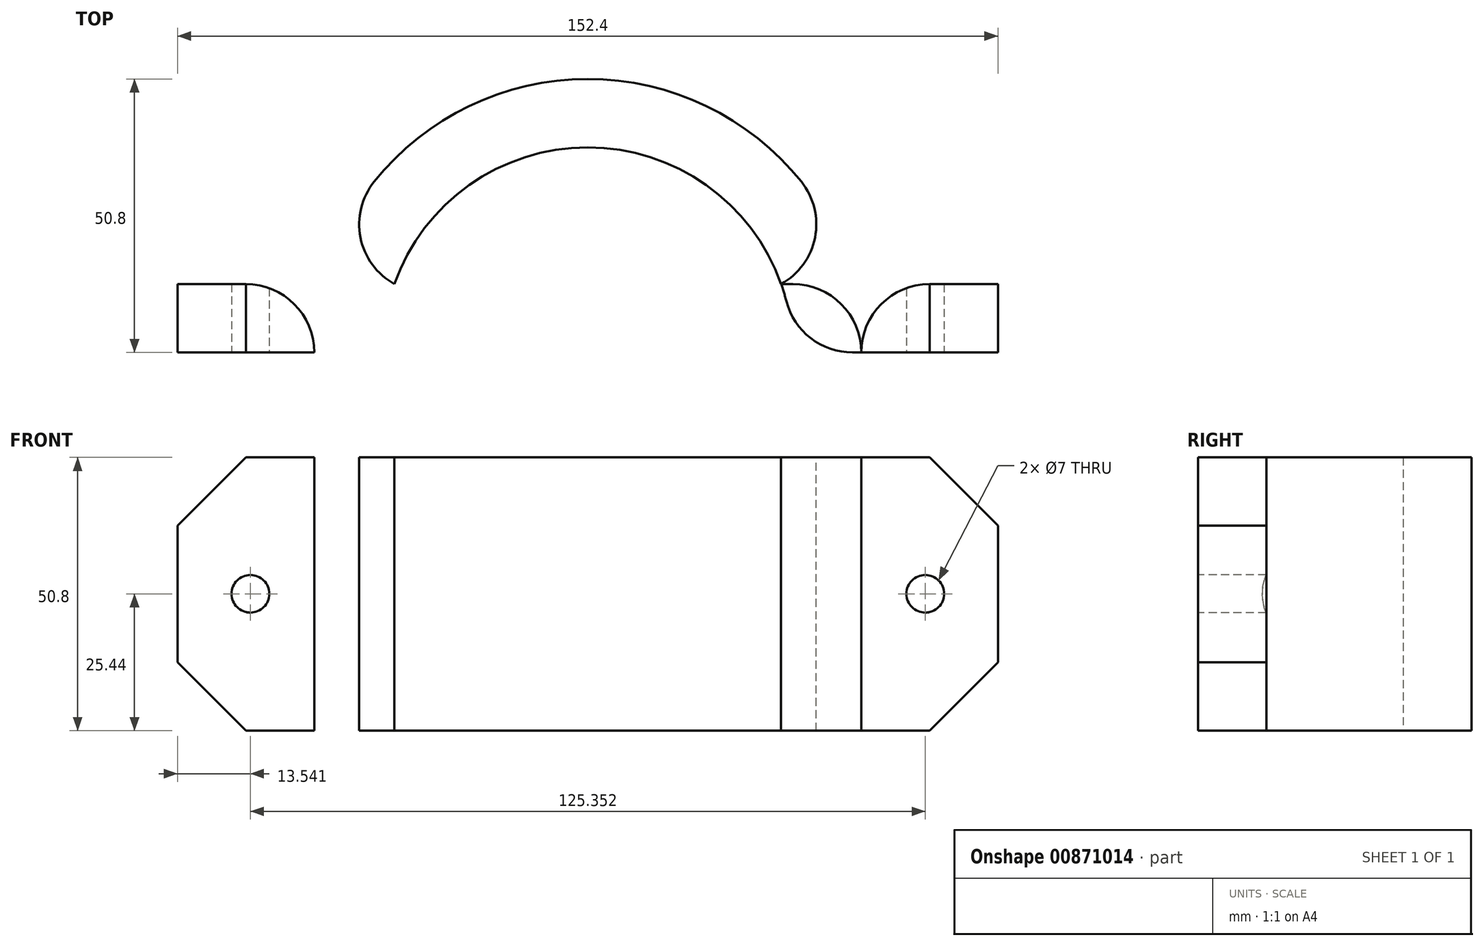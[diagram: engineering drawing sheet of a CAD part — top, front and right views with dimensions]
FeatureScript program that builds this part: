
annotation { "Feature Type Name" : "Feature", "Feature Type Description" : "" }
export const myFeature = defineFeature(function(context is Context, id is Id, definition is map)
    precondition{}
    {
        {
            var Q0;
            Q0=qCreatedBy(makeId("Top.planeOp"),FACE);
            var sketch = newSketch(context, id + "F0", { "sketchPlane" : qUnion([Q0])});
            skCircle(sketch, "E0", {"center": v(0, 0) * mm, "radius": 38.1 * mm});
            skCircle(sketch, "E1", {"center": v(0, 0) * mm, "radius": 50.8 * mm});
            skLineSegment(sketch, "E2.bottom", {"start": v(76.2, -12.7) * mm, "end": v(-76.2, -12.7) * mm});
            skLineSegment(sketch, "E2.top", {"start": v(76.2, 12.7) * mm, "end": v(-76.2, 12.7) * mm});
            skLineSegment(sketch, "E2.left", {"start": v(76.2, -12.7) * mm, "end": v(76.2, 12.7) * mm});
            skLineSegment(sketch, "E2.right", {"start": v(-76.2, -12.7) * mm, "end": v(-76.2, 12.7) * mm});
            skPoint(sketch, "E3", {"position": v(0, -50.8) * mm});
            skLineSegment(sketch, "E4.bottom", {"start": v(19.05, -12.7) * mm, "end": v(-19.05, -12.7) * mm});
            skLineSegment(sketch, "E4.top", {"start": v(19.05, -88.9) * mm, "end": v(-19.05, -88.9) * mm});
            skLineSegment(sketch, "E4.left", {"start": v(19.05, -12.7) * mm, "end": v(19.05, -88.9) * mm});
            skLineSegment(sketch, "E4.right", {"start": v(-19.05, -12.7) * mm, "end": v(-19.05, -88.9) * mm});
            skSolve(sketch);
        }
        {
            var Q0;
            {var subQ0=sQuery(id+"F0.wireOp",EDGE,"E2.top");var subQ1=sQuery(id+"F0.wireOp",EDGE,"E0");var subQ2=makeQuery(id+"F0.imprint","INTERSECT",VERTEX,{"disambiguationData":[OD(0.0)],"derivedFrom":[subQ1,subQ0]});Q0=makeQuery(id+"F0.imprint","IMPRINT",FACE,{"disambiguationData":[TD([[makeQuery(id+"F0.imprint","IMPRINT",EDGE,{"disambiguationData":[TD([[subQ2,1.0]])],"derivedFrom":subQ1}),-1.0]])]});}
            var Q1;
            {var subQ5=sQuery(id+"F0.wireOp",EDGE,"E2.right");Q1=makeQuery(id+"F0.imprint","IMPRINT",FACE,{"disambiguationData":[TD([[makeQuery(id+"F0.imprint","IMPRINT",EDGE,{"derivedFrom":subQ5}),-1.0]])]});}
            var Q2;
            {var subQ0=sQuery(id+"F0.wireOp",EDGE,"E2.top");var subQ1=sQuery(id+"F0.wireOp",EDGE,"E0");var subQ2=makeQuery(id+"F0.imprint","INTERSECT",VERTEX,{"disambiguationData":[OD(0.0)],"derivedFrom":[subQ1,subQ0]});Q2=makeQuery(id+"F0.imprint","IMPRINT",FACE,{"disambiguationData":[TD([[makeQuery(id+"F0.imprint","IMPRINT",EDGE,{"disambiguationData":[TD([[subQ2,-1.0]])],"derivedFrom":subQ1}),-1.0]])]});}
            var Q3;
            {var subQ0=sQuery(id+"F0.wireOp",EDGE,"E2.top");var subQ1=sQuery(id+"F0.wireOp",EDGE,"E0");var subQ2=makeQuery(id+"F0.imprint","INTERSECT",VERTEX,{"disambiguationData":[OD(1.0)],"derivedFrom":[subQ1,subQ0]});Q3=makeQuery(id+"F0.imprint","IMPRINT",FACE,{"disambiguationData":[TD([[makeQuery(id+"F0.imprint","IMPRINT",EDGE,{"disambiguationData":[TD([[subQ2,1.0]])],"derivedFrom":subQ1}),-1.0]])]});}
            var Q4;
            {var subQ5=sQuery(id+"F0.wireOp",EDGE,"E2.left");Q4=makeQuery(id+"F0.imprint","IMPRINT",FACE,{"disambiguationData":[TD([[makeQuery(id+"F0.imprint","IMPRINT",EDGE,{"derivedFrom":subQ5}),1.0]])]});}
            var Q5;
            {var subQ0=sQuery(id+"F0.wireOp",EDGE,"E2.bottom");var subQ1=sQuery(id+"F0.wireOp",EDGE,"E0");var subQ2=makeQuery(id+"F0.imprint","INTERSECT",VERTEX,{"disambiguationData":[OD(0.0)],"derivedFrom":[subQ1,subQ0]});Q5=makeQuery(id+"F0.imprint","IMPRINT",FACE,{"disambiguationData":[TD([[makeQuery(id+"F0.imprint","IMPRINT",EDGE,{"disambiguationData":[TD([[subQ2,-1.0]])],"derivedFrom":subQ1}),-1.0]])]});}
            var Q6;
            {var subQ0=sQuery(id+"F0.wireOp",EDGE,"E4.left");var subQ1=sQuery(id+"F0.wireOp",EDGE,"E0");var subQ2=makeQuery(id+"F0.imprint","INTERSECT",VERTEX,{"derivedFrom":[subQ1,subQ0]});Q6=makeQuery(id+"F0.imprint","IMPRINT",FACE,{"disambiguationData":[TD([[makeQuery(id+"F0.imprint","IMPRINT",EDGE,{"disambiguationData":[TD([[subQ2,-1.0]])],"derivedFrom":subQ1}),-1.0]])]});}
            var Q7;
            {var subQ0=sQuery(id+"F0.wireOp",EDGE,"E4.right");var subQ1=sQuery(id+"F0.wireOp",EDGE,"E0");var subQ2=makeQuery(id+"F0.imprint","INTERSECT",VERTEX,{"derivedFrom":[subQ1,subQ0]});Q7=makeQuery(id+"F0.imprint","IMPRINT",FACE,{"disambiguationData":[TD([[makeQuery(id+"F0.imprint","IMPRINT",EDGE,{"disambiguationData":[TD([[subQ2,-1.0]])],"derivedFrom":subQ1}),-1.0]])]});}
            var Q8;
            {var subQ5=sQuery(id+"F0.wireOp",EDGE,"E4.top");Q8=makeQuery(id+"F0.imprint","IMPRINT",FACE,{"disambiguationData":[TD([[makeQuery(id+"F0.imprint","IMPRINT",EDGE,{"derivedFrom":subQ5}),-1.0]])]});}
            extrude(context, id + "F1", {"entities" : qUnion([Q0, Q1, Q2, Q3, Q4, Q5, Q6, Q7, Q8]), "depth" : 50.8 * mm, "offsetDistance" : 25 * mm});
        }
        {
            var Q0;
            {var subQ0=sQuery(id+"F0.wireOp",EDGE,"E2.bottom");Q0=makeQuery(id+"F1.opExtrude","SWEPT_FACE",FACE,{"disambiguationData":[OSD([subQ0]),TDD([makeQuery(id+"F0.imprint","IMPRINT",EDGE,{"disambiguationData":[TD([[makeQuery(id+"F0.imprint","INTERSECT",VERTEX,{"derivedFrom":[subQ0,sQuery(id+"F0.wireOp",EDGE,"E2.right")]}),1.0]])],"derivedFrom":subQ0})])]});}
            var sketch = newSketch(context, id + "F2", { "sketchPlane" : qUnion([Q0])});
            skPoint(sketch, "E5", {"position": v(-62.7, 25.4) * mm});
            skPoint(sketch, "E5.positionSnap0", {"position": v(-76.2, 25.4) * mm});
            skPoint(sketch, "E5.positionSnap1", {"position": v(-62.7, 50.8) * mm});
            skPoint(sketch, "E6", {"position": v(62.7, 25.4) * mm});
            skCircle(sketch, "E7.cCircle", {"center": v(-62.7, 25.4) * mm, "radius": 7 * mm, "construction": true});
            skLineSegment(sketch, "E7.0", {"start": v(-59.16, 31.44) * mm, "end": v(-55.7, 25.36) * mm});
            skLineSegment(sketch, "E7.1", {"start": v(-55.7, 25.36) * mm, "end": v(-59.23, 19.32) * mm});
            skLineSegment(sketch, "E7.2", {"start": v(-59.23, 19.32) * mm, "end": v(-66.23, 19.36) * mm});
            skLineSegment(sketch, "E7.3", {"start": v(-66.23, 19.36) * mm, "end": v(-69.7, 25.44) * mm});
            skLineSegment(sketch, "E7.4", {"start": v(-69.7, 25.44) * mm, "end": v(-66.16, 31.48) * mm});
            skLineSegment(sketch, "E7.5", {"start": v(-66.16, 31.48) * mm, "end": v(-59.16, 31.44) * mm});
            skCircle(sketch, "E8.cCircle", {"center": v(62.7, 25.4) * mm, "radius": 7 * mm, "construction": true});
            skLineSegment(sketch, "E8.0", {"start": v(55.7, 25.4) * mm, "end": v(59.2, 31.46) * mm});
            skLineSegment(sketch, "E8.1", {"start": v(59.2, 31.46) * mm, "end": v(66.2, 31.46) * mm});
            skLineSegment(sketch, "E8.2", {"start": v(66.2, 31.46) * mm, "end": v(69.7, 25.4) * mm});
            skLineSegment(sketch, "E8.3", {"start": v(69.7, 25.4) * mm, "end": v(66.2, 19.34) * mm});
            skLineSegment(sketch, "E8.4", {"start": v(66.2, 19.34) * mm, "end": v(59.2, 19.34) * mm});
            skLineSegment(sketch, "E8.5", {"start": v(59.2, 19.34) * mm, "end": v(55.7, 25.4) * mm});
            skSolve(sketch);
        }
        {
            var Q0;
            Q0=qSketchRegion(id+"F2",true);
            extrude(context, id + "F3", {"entities" : qUnion([Q0]), "operationType" : NewBodyOperationType.REMOVE, "oppositeDirection" : true, "depth" : 12.7 * mm, "offsetDistance" : 25 * mm});
        }
        {
            var Q0;
            Q0=makeQuery(id+"F1.opExtrude","CAP_EDGE",EDGE,{"disambiguationData":[OSD([sQuery(id+"F0.wireOp",EDGE,"E2.right")])],"isStart":false});
            var Q1;
            Q1=makeQuery(id+"F1.opExtrude","CAP_EDGE",EDGE,{"disambiguationData":[OSD([sQuery(id+"F0.wireOp",EDGE,"E2.right")])],"isStart":true});
            var Q2;
            Q2=makeQuery(id+"F1.opExtrude","CAP_EDGE",EDGE,{"disambiguationData":[OSD([sQuery(id+"F0.wireOp",EDGE,"E2.left")])],"isStart":false});
            var Q3;
            Q3=makeQuery(id+"F1.opExtrude","CAP_EDGE",EDGE,{"disambiguationData":[OSD([sQuery(id+"F0.wireOp",EDGE,"E2.left")])],"isStart":true});
            chamfer(context, id + "F4", {"entities" : qUnion([Q0, Q1, Q2, Q3]), "width" : 12.7 * mm, "tangentPropagation" : true});
        }
        {
            var Q0;
            Q0=makeQuery(id+"F1.opExtrude","CAP_FACE",FACE,{"disambiguationData":[OSD([sQuery(id+"F0.wireOp",EDGE,"E0"),sQuery(id+"F0.wireOp",EDGE,"E1"),sQuery(id+"F0.wireOp",EDGE,"E2.bottom"),sQuery(id+"F0.wireOp",EDGE,"E2.top"),sQuery(id+"F0.wireOp",EDGE,"E2.left"),sQuery(id+"F0.wireOp",EDGE,"E2.right"),sQuery(id+"F0.wireOp",EDGE,"E4.top"),sQuery(id+"F0.wireOp",EDGE,"E4.left"),sQuery(id+"F0.wireOp",EDGE,"E4.right")])],"isStart":false});
            var sketch = newSketch(context, id + "F5", { "sketchPlane" : qUnion([Q0])});
            skPoint(sketch, "E9", {"position": v(0, -68) * mm});
            skPoint(sketch, "E9.positionSnap0", {"position": v(-19.05, -68) * mm});
            skPoint(sketch, "E9.positionSnap1", {"position": v(0, -88.9) * mm});
            skCircle(sketch, "E10", {"center": v(0, -68) * mm, "radius": 11.35 * mm});
            skCircle(sketch, "E11", {"center": v(0, -68) * mm, "radius": 10 * mm});
            skSolve(sketch);
        }
        {
            var Q0;
            Q0=makeQuery(id+"F5.imprint","IMPRINT",FACE,{"disambiguationData":[TD([[makeQuery(id+"F5.imprint","IMPRINT",EDGE,{"derivedFrom":sQuery(id+"F5.wireOp",EDGE,"E10")}),1.0]])]});
            var Q1;
            Q1=sQuery(id+"F5.wireOp",EDGE,"E11");
            var Q2;
            Q2=sQuery(id+"F5.wireOp",EDGE,"E10");
            extrude(context, id + "F6", {"entities" : qUnion([Q0]), "operationType" : NewBodyOperationType.REMOVE, "surfaceEntities" : qUnion([Q1, Q2]), "oppositeDirection" : true, "depth" : 44.45 * mm, "offsetDistance" : 25 * mm});
        }
        {
            var Q0;
            Q0=makeQuery(id+"F1.opExtrude","SWEPT_EDGE",EDGE,{"disambiguationData":[OSD([sQuery(id+"F0.wireOp",EDGE,"E4.top"),sQuery(id+"F0.wireOp",EDGE,"E4.right")])]});
            var Q1;
            Q1=makeQuery(id+"F1.opExtrude","SWEPT_EDGE",EDGE,{"disambiguationData":[OSD([sQuery(id+"F0.wireOp",EDGE,"E4.top"),sQuery(id+"F0.wireOp",EDGE,"E4.left")])]});
            var Q2;
            Q2=makeQuery(id+"F1.opExtrude","SWEPT_EDGE",EDGE,{"disambiguationData":[OSD([sQuery(id+"F0.wireOp",EDGE,"E1"),sQuery(id+"F0.wireOp",EDGE,"E4.right")])]});
            var Q3;
            Q3=makeQuery(id+"F1.opExtrude","SWEPT_EDGE",EDGE,{"disambiguationData":[OSD([sQuery(id+"F0.wireOp",EDGE,"E1"),sQuery(id+"F0.wireOp",EDGE,"E4.left")])]});
            var Q4;
            {var subQ0=sQuery(id+"F0.wireOp",EDGE,"E2.bottom");var subQ1=sQuery(id+"F0.wireOp",EDGE,"E1");Q4=makeQuery(id+"F1.opExtrude","SWEPT_EDGE",EDGE,{"disambiguationData":[OSD([subQ1,subQ0]),TDD([makeQuery(id+"F0.imprint","INTERSECT",VERTEX,{"disambiguationData":[OD(1.0)],"derivedFrom":[subQ1,subQ0]})])]});}
            var Q5;
            {var subQ0=sQuery(id+"F0.wireOp",EDGE,"E2.bottom");var subQ1=sQuery(id+"F0.wireOp",EDGE,"E1");Q5=makeQuery(id+"F1.opExtrude","SWEPT_EDGE",EDGE,{"disambiguationData":[OSD([subQ1,subQ0]),TDD([makeQuery(id+"F0.imprint","INTERSECT",VERTEX,{"disambiguationData":[OD(0.0)],"derivedFrom":[subQ1,subQ0]})])]});}
            var Q6;
            {var subQ0=sQuery(id+"F0.wireOp",EDGE,"E2.top");var subQ1=sQuery(id+"F0.wireOp",EDGE,"E1");Q6=makeQuery(id+"F1.opExtrude","SWEPT_EDGE",EDGE,{"disambiguationData":[OSD([subQ1,subQ0]),TDD([makeQuery(id+"F0.imprint","INTERSECT",VERTEX,{"disambiguationData":[OD(1.0)],"derivedFrom":[subQ1,subQ0]})])]});}
            var Q7;
            {var subQ0=sQuery(id+"F0.wireOp",EDGE,"E2.top");var subQ1=sQuery(id+"F0.wireOp",EDGE,"E1");Q7=makeQuery(id+"F1.opExtrude","SWEPT_EDGE",EDGE,{"disambiguationData":[OSD([subQ1,subQ0]),TDD([makeQuery(id+"F0.imprint","INTERSECT",VERTEX,{"disambiguationData":[OD(0.0)],"derivedFrom":[subQ1,subQ0]})])]});}
            fillet(context, id + "F7", {"entities" : qUnion([Q0, Q1, Q2, Q3, Q4, Q5, Q6, Q7]), "radius" : 12.7 * mm, "tangentPropagation" : true, "allowEdgeOverflow" : false});
        }
        {
            var Q0;
            Q0=makeQuery(id+"F3.boolean.opBoolean","COPY",FACE,{"derivedFrom":makeQuery(id+"F3.opExtrude","CAP_FACE",FACE,{"disambiguationData":[OSD([sQuery(id+"F2.wireOp",EDGE,"E7.0"),sQuery(id+"F2.wireOp",EDGE,"E7.1"),sQuery(id+"F2.wireOp",EDGE,"E7.2"),sQuery(id+"F2.wireOp",EDGE,"E7.3"),sQuery(id+"F2.wireOp",EDGE,"E7.4"),sQuery(id+"F2.wireOp",EDGE,"E7.5")])],"isStart":false})});
            var sketch = newSketch(context, id + "F8", { "sketchPlane" : qUnion([Q0])});
            skPoint(sketch, "E12", {"position": v(-62.66, 25.44) * mm});
            skPoint(sketch, "E12.positionSnap0", {"position": v(-62.66, 31.46) * mm});
            skPoint(sketch, "E13", {"position": v(62.7, 25.44) * mm});
            skPoint(sketch, "E14", {"position": v(62.7, 31.46) * mm});
            skCircle(sketch, "E15", {"center": v(-62.66, 25.44) * mm, "radius": 3.5 * mm});
            skCircle(sketch, "E16", {"center": v(62.7, 25.44) * mm, "radius": 3.5 * mm});
            skSolve(sketch);
        }
        {
            var Q0;
            Q0=makeQuery(id+"F8.imprint","IMPRINT",FACE,{"disambiguationData":[TD([[makeQuery(id+"F8.imprint","IMPRINT",EDGE,{"derivedFrom":sQuery(id+"F8.wireOp",EDGE,"E15")}),1.0]])]});
            var Q1;
            Q1=makeQuery(id+"F8.imprint","IMPRINT",FACE,{"disambiguationData":[TD([[makeQuery(id+"F8.imprint","IMPRINT",EDGE,{"derivedFrom":sQuery(id+"F8.wireOp",EDGE,"E16")}),1.0]])]});
            extrude(context, id + "F9", {"entities" : qUnion([Q0, Q1]), "operationType" : NewBodyOperationType.REMOVE, "endBound" : BoundingType.THROUGH_ALL, "oppositeDirection" : true, "depth" : 25 * mm, "offsetDistance" : 25 * mm});
        }
        {
            var Q0;
            Q0=qCreatedBy(makeId("Front.planeOp"),FACE);
            var sketch = newSketch(context, id + "F10", { "sketchPlane" : qUnion([Q0])});
            skLineSegment(sketch, "E17.bottom", {"start": v(-97.94, 76.17) * mm, "end": v(85.9, 76.17) * mm});
            skLineSegment(sketch, "E17.top", {"start": v(-97.94, -81.22) * mm, "end": v(85.9, -81.22) * mm});
            skLineSegment(sketch, "E17.left", {"start": v(-97.94, 76.17) * mm, "end": v(-97.94, -81.22) * mm});
            skLineSegment(sketch, "E17.right", {"start": v(85.9, 76.17) * mm, "end": v(85.9, -81.22) * mm});
            skSolve(sketch);
        }
        {
            var Q0;
            Q0=qSketchRegion(id+"F10",true);
            extrude(context, id + "F11", {"entities" : qUnion([Q0]), "operationType" : NewBodyOperationType.REMOVE, "depth" : 114.3 * mm, "offsetDistance" : 25 * mm});
        }
        {
            var Q0;
            {var subQ0=makeQuery(id+"F1.opExtrude","SWEPT_FACE",FACE,{"disambiguationData":[OSD([sQuery(id+"F0.wireOp",EDGE,"E0")])]});var subQ1=makeQuery(id+"F11.opExtrude","CAP_FACE",FACE,{"disambiguationData":[OSD([sQuery(id+"F10.wireOp",EDGE,"E17.bottom"),sQuery(id+"F10.wireOp",EDGE,"E17.top"),sQuery(id+"F10.wireOp",EDGE,"E17.left"),sQuery(id+"F10.wireOp",EDGE,"E17.right")])],"isStart":true});Q0=makeQuery(id+"F11.boolean.opBoolean","INTERSECT",EDGE,{"disambiguationData":[topologyDisambiguationEdgeConnected([makeQuery(id+"F3.boolean.opBoolean","COPY",FACE,{"derivedFrom":makeQuery(id+"F3.opExtrude","CAP_FACE",FACE,{"disambiguationData":[OSD([sQuery(id+"F2.wireOp",EDGE,"E7.0"),sQuery(id+"F2.wireOp",EDGE,"E7.1"),sQuery(id+"F2.wireOp",EDGE,"E7.2"),sQuery(id+"F2.wireOp",EDGE,"E7.3"),sQuery(id+"F2.wireOp",EDGE,"E7.4"),sQuery(id+"F2.wireOp",EDGE,"E7.5")])],"isStart":false})})])],"derivedFrom":[subQ0,subQ1]});}
            var Q1;
            {var subQ0=makeQuery(id+"F1.opExtrude","SWEPT_FACE",FACE,{"disambiguationData":[OSD([sQuery(id+"F0.wireOp",EDGE,"E0")])]});var subQ1=makeQuery(id+"F11.opExtrude","CAP_FACE",FACE,{"disambiguationData":[OSD([sQuery(id+"F10.wireOp",EDGE,"E17.bottom"),sQuery(id+"F10.wireOp",EDGE,"E17.top"),sQuery(id+"F10.wireOp",EDGE,"E17.left"),sQuery(id+"F10.wireOp",EDGE,"E17.right")])],"isStart":true});Q1=makeQuery(id+"F11.boolean.opBoolean","INTERSECT",EDGE,{"disambiguationData":[topologyDisambiguationEdgeConnected([makeQuery(id+"F3.boolean.opBoolean","COPY",FACE,{"derivedFrom":makeQuery(id+"F3.opExtrude","CAP_FACE",FACE,{"disambiguationData":[OSD([sQuery(id+"F2.wireOp",EDGE,"E8.0"),sQuery(id+"F2.wireOp",EDGE,"E8.1"),sQuery(id+"F2.wireOp",EDGE,"E8.2"),sQuery(id+"F2.wireOp",EDGE,"E8.3"),sQuery(id+"F2.wireOp",EDGE,"E8.4"),sQuery(id+"F2.wireOp",EDGE,"E8.5")])],"isStart":false})})])],"derivedFrom":[subQ0,subQ1]});}
            fillet(context, id + "F12", {"entities" : qUnion([Q0, Q1]), "radius" : 12.7 * mm, "tangentPropagation" : true, "allowEdgeOverflow" : false});
        }
    });
